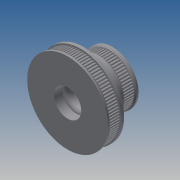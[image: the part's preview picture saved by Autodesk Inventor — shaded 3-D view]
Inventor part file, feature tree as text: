
AUTODESK INVENTOR PART (.ipt)
format: ipt  version: 2013 (Build 170138000, 138)  size: 931,328 bytes
history: native  units: mm
features: extrude x10, sketch x10, pattern_circular x2, chamfer x2, mirror x1, fillet x1
ambient origin geometry x8: Origin, YZ Plane, XZ Plane, XY Plane, X Axis, Y Axis, Z Axis, Center Point
bodies: Solid1 (feature_tree)
feature tree (26):
  extrude  "Extrusion1"  Depth=8.0mm TaperAngle=0.0deg
  extrude  "Extrusion2"  Depth=8.0mm TaperAngle=0.0deg
  pattern_circular  "Circular Pattern1"  Count=100 Angle=360.0deg
  extrude  "Extrusion3"  Depth=2.5mm TaperAngle=0.0deg
  chamfer  "Chamfer1"  Distance=1.0mm Angle=45.0deg
  mirror  "Mirror1"
  extrude  "Extrusion4"  Depth=23.1mm TaperAngle=0.0deg
  extrude  "Extrusion5"  Depth=23.1mm TaperAngle=0.0deg
  pattern_circular  "Circular Pattern2"  Count=64 Angle=360.0deg
  extrude  "Extrusion6"  Depth=12.6mm TaperAngle=0.0deg
  extrude  "Extrusion7"  Depth=1.0mm TaperAngle=45.0deg
  chamfer  "Chamfer2"  Distance=2.5mm
  extrude  "Extrusion8"  Depth=7.0mm TaperAngle=0.0deg
  extrude  "Extrusion9"  Depth=7.0mm TaperAngle=0.0deg
  extrude  "Extrusion10"  Depth=3.5mm
  fillet  "Fillet1"  [1 undecoded]
  sketch  "Sketch1"  dims[d0=63.153977mm d3=8.0mm d4=0.0mm]
  sketch  "Sketch2"  dims[d5=1.59mm d7=8.0mm d8=0.0mm d9=1000.0mm d10=360.0deg]
  sketch  "Sketch4"  dims[d12=1.0mm d13=2.5mm d14=0.0mm d15=1.0mm d16=2.0mm d17=45.0deg]
  sketch  "Sketch5"  dims[d18=40.235665mm d20=23.1mm d21=0.0mm]
  sketch  "Sketch6"  dims[d22=1.59mm d24=23.1mm d25=0.0mm d26=640.0mm d27=360.0deg]
  sketch  "Sketch7"  dims[d29=1.0mm d30=12.6mm d31=0.0mm]
  sketch  "Sketch8"  dims[d32=2.5mm d33=0.0mm d34=1.0mm d35=2.0mm d36=45.0deg]
  sketch  "Sketch9"  dims[d37=15.0mm d39=2.5mm d40=0.0mm]
  sketch  "Sketch10"  dims[d41=22.0mm d43=7.0mm d44=0.0mm]
  sketch  "Sketch11"  dims[d45=22.0mm d47=7.0mm d48=0.0mm d49=3.5mm]
note: 1 required parameter value undecoded (feature->parameter linkage not recoverable at this tier; creation-order binding heuristic only, values carry confidence <= 0.55)
